# Revit family: Plumbing Fixture-FloorDrain_Mifab_C1450-S
name_source: partatom
category: Plumbing Fixtures
revit_build: Autodesk Revit Structure 2013 (Build: 20120221_2030(x64)
units: mm (PartAtom-declared; Revit-internal decimal feet)

## types (3) — shared parameters
Body Height = 2.2 "
Floor Drain Material = Paint - Sherwin Williams Paint - #952C2A - Bellwood Red
Manufacturer = MIFAB
Model = C1450-S
Stainer Diameter = 8.3 "
Strainer Radius = 4.15 "
Top Assembly Height = 4 "
URL = WWW.MIFAB.COM
zero-valued in all types: Default Elevation, WFU

## per-type parameters (varying)
| type | Description | HEIGHT 1 | Pipe Diameter | Pipe Radius |
| 3" | LINE CLEANOUT WITH SQUARE, NICKEL BRONZE WALL ACCESS PANEL | 5.282 " | 3 " | 1.5 " |
| 2" | LINE CLEANOUT WITH SQUARE, NICKEL BRONZE WALL ACCESS PANEL
BRONZE WALL ACCESS PANEL | 5.4 " | 2 " | 1 " |
| 4" | LINE CLEANOUT WITH SQUARE, NICKEL BRONZE WALL ACCESS PANEL | 5.282 " | 4 " | 2 " |

## geometry (parser evidence)
native form markers: Blend x3, Sweep x1
no freeform markers — native parametric forms only
